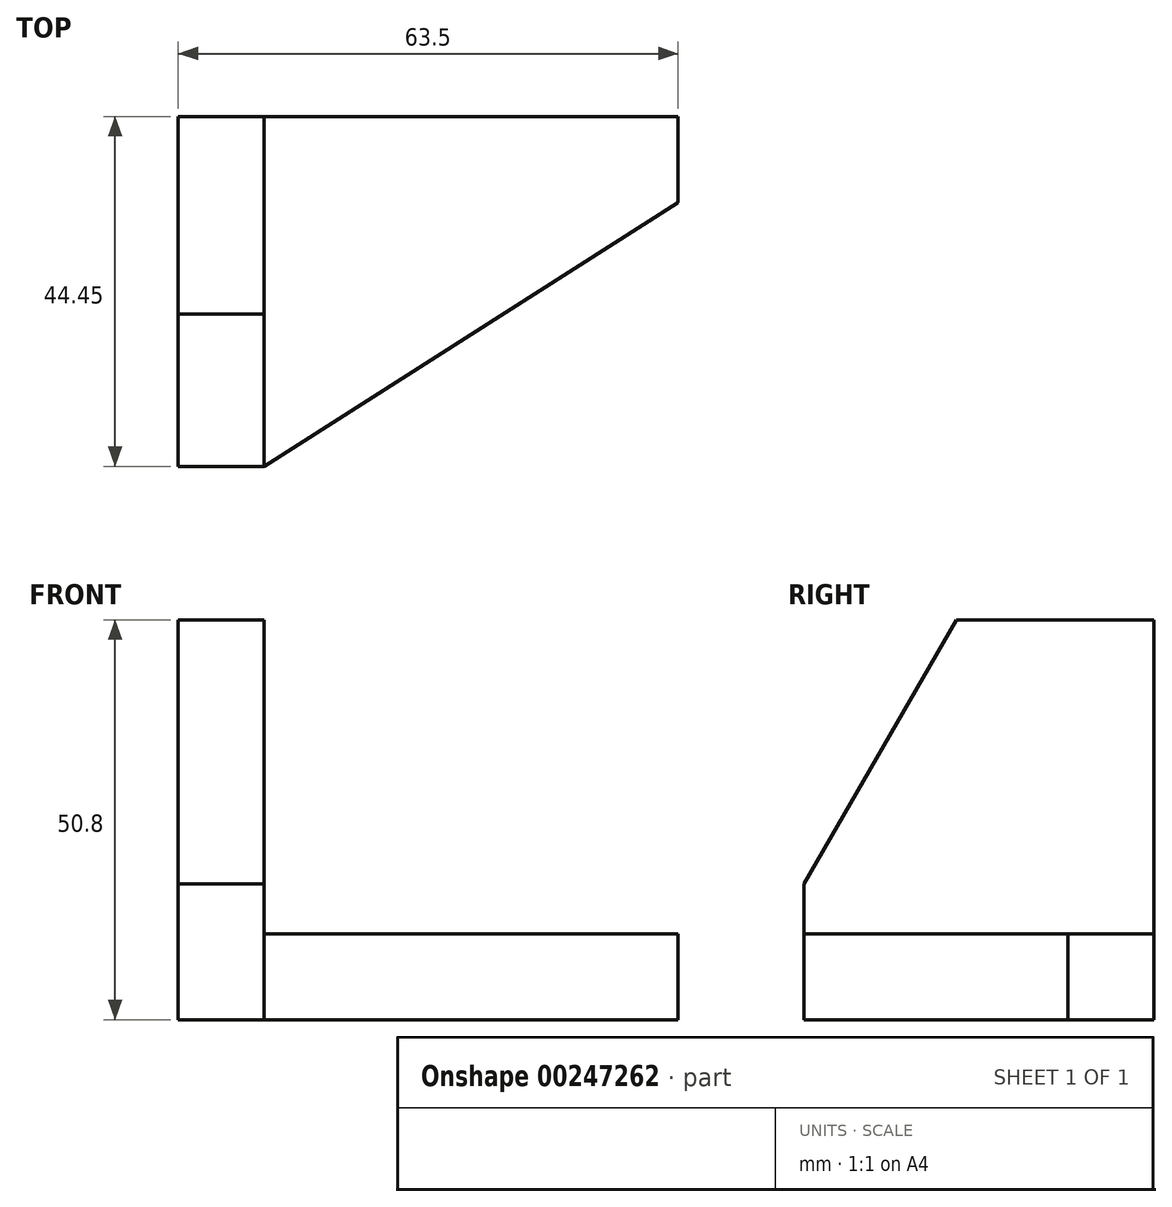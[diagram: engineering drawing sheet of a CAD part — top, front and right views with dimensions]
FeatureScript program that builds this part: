
annotation { "Feature Type Name" : "Feature", "Feature Type Description" : "" }
export const myFeature = defineFeature(function(context is Context, id is Id, definition is map)
    precondition{}
    {
        {
            var Q0;
            Q0=qCreatedBy(makeId("Front.planeOp"),FACE);
            var sketch = newSketch(context, id + "F0", { "sketchPlane" : qUnion([Q0])});
            skLineSegment(sketch, "E0.bottom", {"start": v(0, 30.1) * mm, "end": v(31.75, 30.1) * mm});
            skLineSegment(sketch, "E0.top", {"start": v(0, -30.1) * mm, "end": v(114.3, -30.1) * mm});
            skLineSegment(sketch, "E0.left", {"start": v(0, 30.1) * mm, "end": v(0, -30.1) * mm});
            skLineSegment(sketch, "E0.right", {"start": v(114.3, 7.98) * mm, "end": v(114.3, -30.1) * mm});
            skLineSegment(sketch, "E1", {"start": v(31.75, 30.1) * mm, "end": v(114.3, 7.98) * mm});
            skCircle(sketch, "E2", {"center": v(95.25, -11.05) * mm, "radius": 7.87 * mm});
            skLineSegment(sketch, "E3.bottom", {"start": v(0, -30.1) * mm, "end": v(10.92, -30.1) * mm});
            skLineSegment(sketch, "E3.top", {"start": v(0, 20.7) * mm, "end": v(10.92, 20.7) * mm});
            skLineSegment(sketch, "E3.left", {"start": v(0, -30.1) * mm, "end": v(0, 20.7) * mm});
            skLineSegment(sketch, "E3.right", {"start": v(10.92, -30.1) * mm, "end": v(10.92, 20.7) * mm});
            skLineSegment(sketch, "E4.top", {"start": v(0, -8) * mm, "end": v(10.92, -8) * mm});
            skLineSegment(sketch, "E4.left", {"start": v(0, -30.1) * mm, "end": v(0, -8) * mm});
            skLineSegment(sketch, "E4.right", {"start": v(10.92, -30.1) * mm, "end": v(10.92, -8) * mm});
            skLineSegment(sketch, "E5.bottom", {"start": v(0, -30.1) * mm, "end": v(63.5, -30.1) * mm});
            skLineSegment(sketch, "E5.top", {"start": v(10.92, -19.18) * mm, "end": v(63.5, -19.18) * mm});
            skLineSegment(sketch, "E5.left", {"start": v(0, -30.1) * mm, "end": v(0, -19.18) * mm});
            skLineSegment(sketch, "E5.right", {"start": v(63.5, -30.1) * mm, "end": v(63.5, -19.18) * mm});
            skLineSegment(sketch, "E6", {"start": v(31.75, 30.1) * mm, "end": v(114.3, 30.1) * mm, "construction": true});
            skLineSegment(sketch, "E7", {"start": v(114.3, 30.1) * mm, "end": v(114.3, 7.98) * mm, "construction": true});
            skSolve(sketch);
        }
        {
            var Q0;
            {var subQ6=sQuery(id+"F0.wireOp",EDGE,"E0.top");Q0=makeQuery(id+"F0.imprint","IMPRINT",FACE,{"disambiguationData":[TD([[makeQuery(id+"F0.imprint","IMPRINT",EDGE,{"derivedFrom":subQ6}),1.0]])]});}
            extrude(context, id + "F1", {"entities" : qUnion([Q0]), "depth" : 10.92 * mm});
        }
        {
            var Q0;
            Q0=makeQuery(id+"F0.imprint","IMPRINT",FACE,{"disambiguationData":[TD([[makeQuery(id+"F0.imprint","IMPRINT",EDGE,{"derivedFrom":sQuery(id+"F0.wireOp",EDGE,"E3.top")}),-1.0]])]});
            var Q1;
            {var subQ1=sQuery(id+"F0.wireOp",EDGE,"E4.top");Q1=makeQuery(id+"F0.imprint","IMPRINT",FACE,{"disambiguationData":[TD([[makeQuery(id+"F0.imprint","IMPRINT",EDGE,{"derivedFrom":subQ1}),-1.0]])]});}
            var Q2;
            {var subQ3=sQuery(id+"F0.wireOp",EDGE,"E5.top");Q2=makeQuery(id+"F0.imprint","IMPRINT",FACE,{"disambiguationData":[TD([[makeQuery(id+"F0.imprint","IMPRINT",EDGE,{"derivedFrom":subQ3}),-1.0]])]});}
            extrude(context, id + "F2", {"entities" : qUnion([Q0, Q1, Q2]), "operationType" : NewBodyOperationType.ADD, "depth" : 44.45 * mm});
        }
        {
            var Q0;
            Q0=makeQuery(id+"F2.opExtrude","CAP_EDGE",EDGE,{"disambiguationData":[OSD([sQuery(id+"F0.wireOp",EDGE,"E5.right")])],"isStart":false});
            chamfer(context, id + "F3", {"entities" : qUnion([Q0]), "chamferType" : ChamferType.TWO_OFFSETS, "width1" : 52.58 * mm, "oppositeDirection" : false, "width2" : 33.53 * mm, "tangentPropagation" : true});
        }
        {
            var Q0;
            Q0=makeQuery(id+"F2.opExtrude","CAP_EDGE",EDGE,{"disambiguationData":[OSD([sQuery(id+"F0.wireOp",EDGE,"E3.top")])],"isStart":false});
            chamfer(context, id + "F4", {"entities" : qUnion([Q0]), "chamferType" : ChamferType.OFFSET_ANGLE, "width" : 33.53 * mm, "oppositeDirection" : true, "angle" : 30 * degree, "tangentPropagation" : true});
        }
    });
